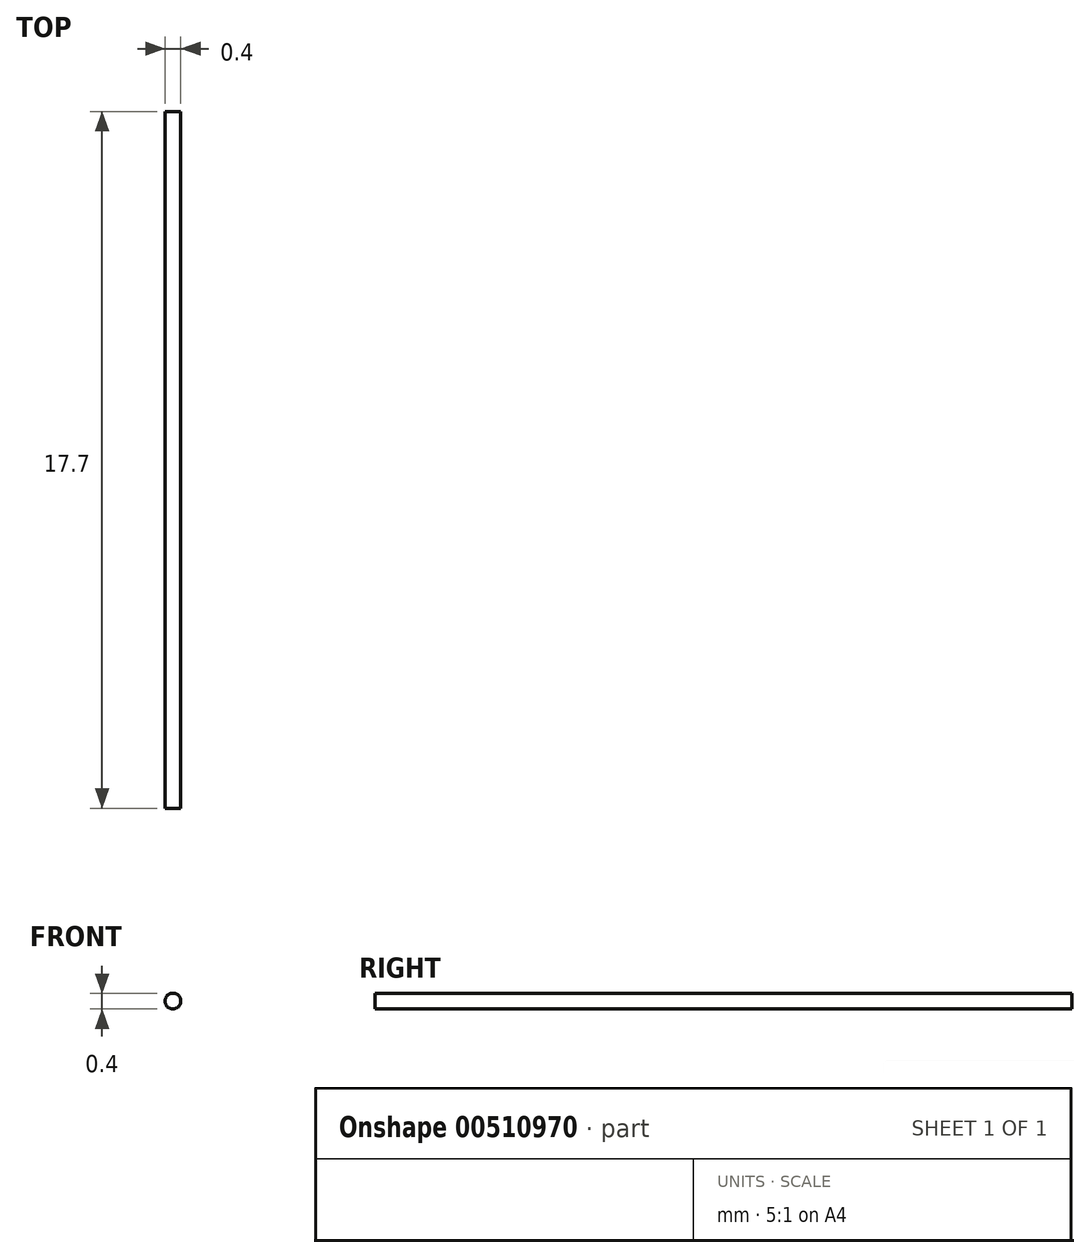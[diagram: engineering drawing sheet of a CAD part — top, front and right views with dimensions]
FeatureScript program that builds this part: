
annotation { "Feature Type Name" : "Feature", "Feature Type Description" : "" }
export const myFeature = defineFeature(function(context is Context, id is Id, definition is map)
    precondition{}
    {
        {
            var Q0;
            Q0=qCreatedBy(makeId("Front.planeOp"),FACE);
            var sketch = newSketch(context, id + "F0", { "sketchPlane" : qUnion([Q0])});
            skCircle(sketch, "E0", {"center": v(-32.1, 16.8) * mm, "radius": 0.2 * mm});
            skSolve(sketch);
        }
        {
            var Q0;
            Q0=makeQuery(id+"F0.imprint","IMPRINT",FACE,{"disambiguationData":[TD([[makeQuery(id+"F0.imprint","IMPRINT",EDGE,{"derivedFrom":sQuery(id+"F0.wireOp",EDGE,"E0")}),1.0]])]});
            extrude(context, id + "F1", {"entities" : qUnion([Q0]), "depth" : 17.7 * mm, "offsetDistance" : 25 * mm});
        }
    });
